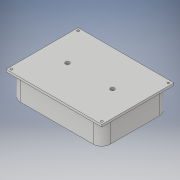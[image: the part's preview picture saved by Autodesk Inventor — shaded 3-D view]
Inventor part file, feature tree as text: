
AUTODESK INVENTOR PART (.ipt)
format: ipt  version: 2018 (Build 220112000, 112)  size: 312,320 bytes
history: native  units: in
note: dims shown in document units (in); Inventor stores cm internally (conversion verified against a paired STEP export)
features: extrude x11, sketch x7, projected_geometry x7, fillet x1, chamfer x1
ambient origin geometry x8: Origin, YZ Plane, XZ Plane, XY Plane, X Axis, Y Axis, Z Axis, Center Point
bodies: Solid1 (feature_tree)
feature tree (27):
  sketch  "Sketch1"  dims[d0=9.125in d1=0.5in]
  extrude  "Extrusion1"  Depth=0.5in
  extrude  "Extrusion2"  Depth=0.25in
  fillet  "Fillet1"  Radius=0.25in
  sketch  "Sketch2"  dims[d2=0.5in d3=6.5in d4=0.25in]
  extrude  "Extrusion3"  Depth=2.3622in TaperAngle=0.0deg
  extrude  "Extrusion4"  Depth=1.0in
  extrude  "Extrusion5"  Depth=0.5in
  extrude  "Extrusion6"  Depth=0.5in
  sketch  "Sketch5"  dims[d11=2.25in d12=0.5in]
  extrude  "Extrusion7"  Depth=0.5in
  extrude  "Extrusion8"  Depth=0.5in
  extrude  "Extrusion9"  Depth=2.179in
  extrude  "Extrusion10"  Depth=1.0in TaperAngle=0.0deg
  chamfer  "Chamfer2"  Distance=0.125in
  extrude  "Extrusion11"  Depth=1.0in
  sketch  "Sketch3"  dims[d5=2.3622in d6=0.0in d7=0.6in d8=0.0in]
  projected_geometry  "Projected Loop1"
  sketch  "Sketch4"  dims[d9=1.0in d10=3.5in]
  projected_geometry  "Projected Loop2"
  projected_geometry  "Projected Loop3"
  projected_geometry  "Projected Loop4"
  projected_geometry  "Projected Loop5"
  projected_geometry  "Projected Loop6"
  sketch  "Sketch6"  dims[d13=0.5in d14=0.5in]
  sketch  "Sketch7"  dims[d15=0.5in d17=0.5in d18=0.5in d19=0.45in d20=1.0in d21=0.0in d22=0.125in d23=0.0in d24=1.0in d25=1.0in d26=1.0in d27=0.125in d28=0.0in d29=0.125in d30=0.0in d31=0.25in d32=0.3in d33=0.3in d34=0.3in d35=0.3in d36=1.0in d37=0.0in d38=0.25in d39=0.0in d40=0.25in d41=0.0in d42=2.5in d43=2.5in d44=0.45in d45=0.45in d46=0.25in d47=0.0in d51=0.0625in d52=0.125in d53=45.0deg d54=0.375in d55=2.179in d56=0.0in]
  projected_geometry  "Projected Loop7"
